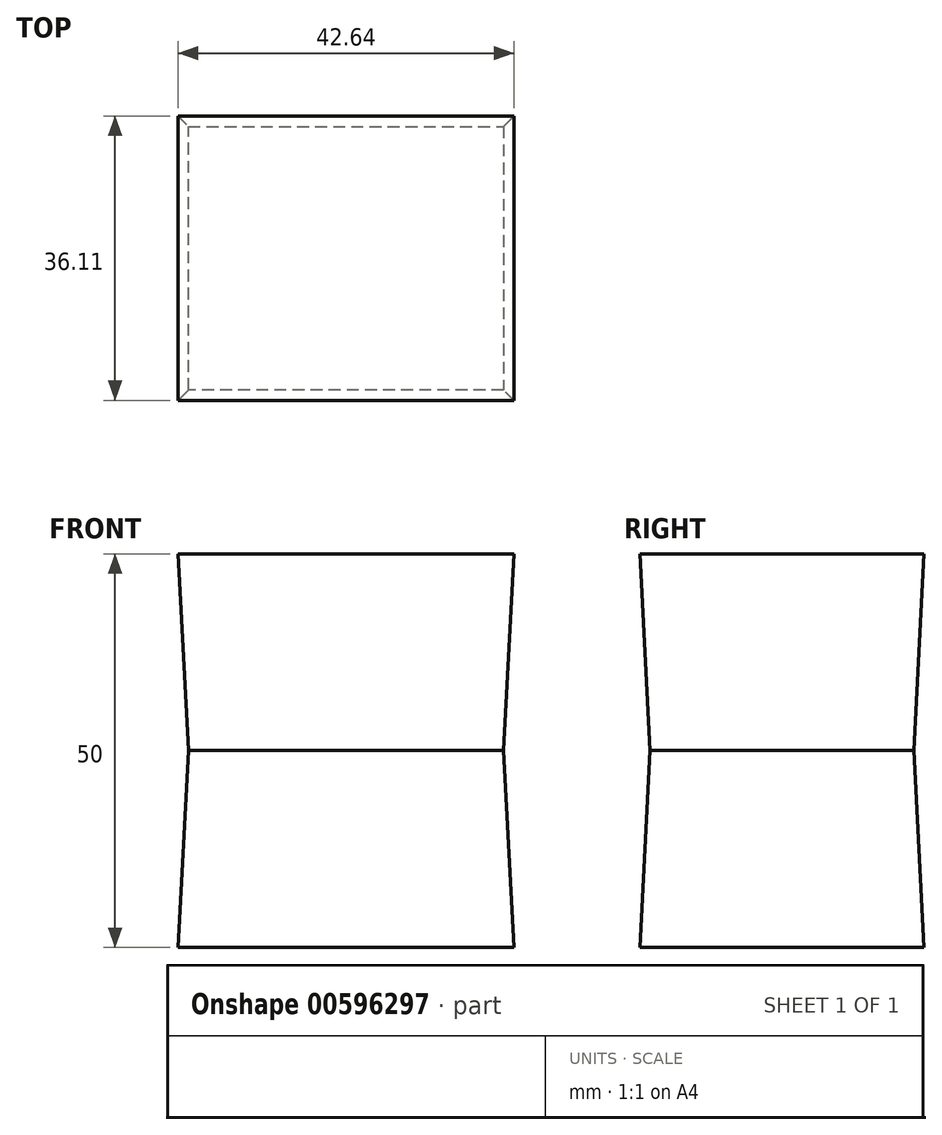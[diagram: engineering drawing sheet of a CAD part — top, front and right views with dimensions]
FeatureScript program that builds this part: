
annotation { "Feature Type Name" : "Feature", "Feature Type Description" : "" }
export const myFeature = defineFeature(function(context is Context, id is Id, definition is map)
    precondition{}
    {
        {
            var Q0;
            Q0=qCreatedBy(makeId("Top.planeOp"),FACE);
            var sketch = newSketch(context, id + "F0", { "sketchPlane" : qUnion([Q0])});
            skLineSegment(sketch, "E0.bottom", {"start": v(0, 0) * mm, "end": v(40.02, 0) * mm});
            skLineSegment(sketch, "E0.top", {"start": v(0, 33.49) * mm, "end": v(40.02, 33.49) * mm});
            skLineSegment(sketch, "E0.left", {"start": v(0, 0) * mm, "end": v(0, 33.49) * mm});
            skLineSegment(sketch, "E0.right", {"start": v(40.02, 0) * mm, "end": v(40.02, 33.49) * mm});
            skSolve(sketch);
        }
        {
            var Q0;
            Q0=makeQuery(id+"F0.imprint","IMPRINT",FACE,{"disambiguationData":[TD([[makeQuery(id+"F0.imprint","IMPRINT",EDGE,{"derivedFrom":sQuery(id+"F0.wireOp",EDGE,"E0.bottom")}),1.0]])]});
            var Q1;
            Q1 = qSketchRegion(id + "F0", true);
            extrude(context, id + "F1", {"entities" : qUnion([Q0, Q1]), "endBound" : BoundingType.SYMMETRIC, "depth" : 50 * mm, "offsetDistance" : 25 * mm, "hasDraft" : true, "draftAngle" : 3 * degree});
        }
    });
